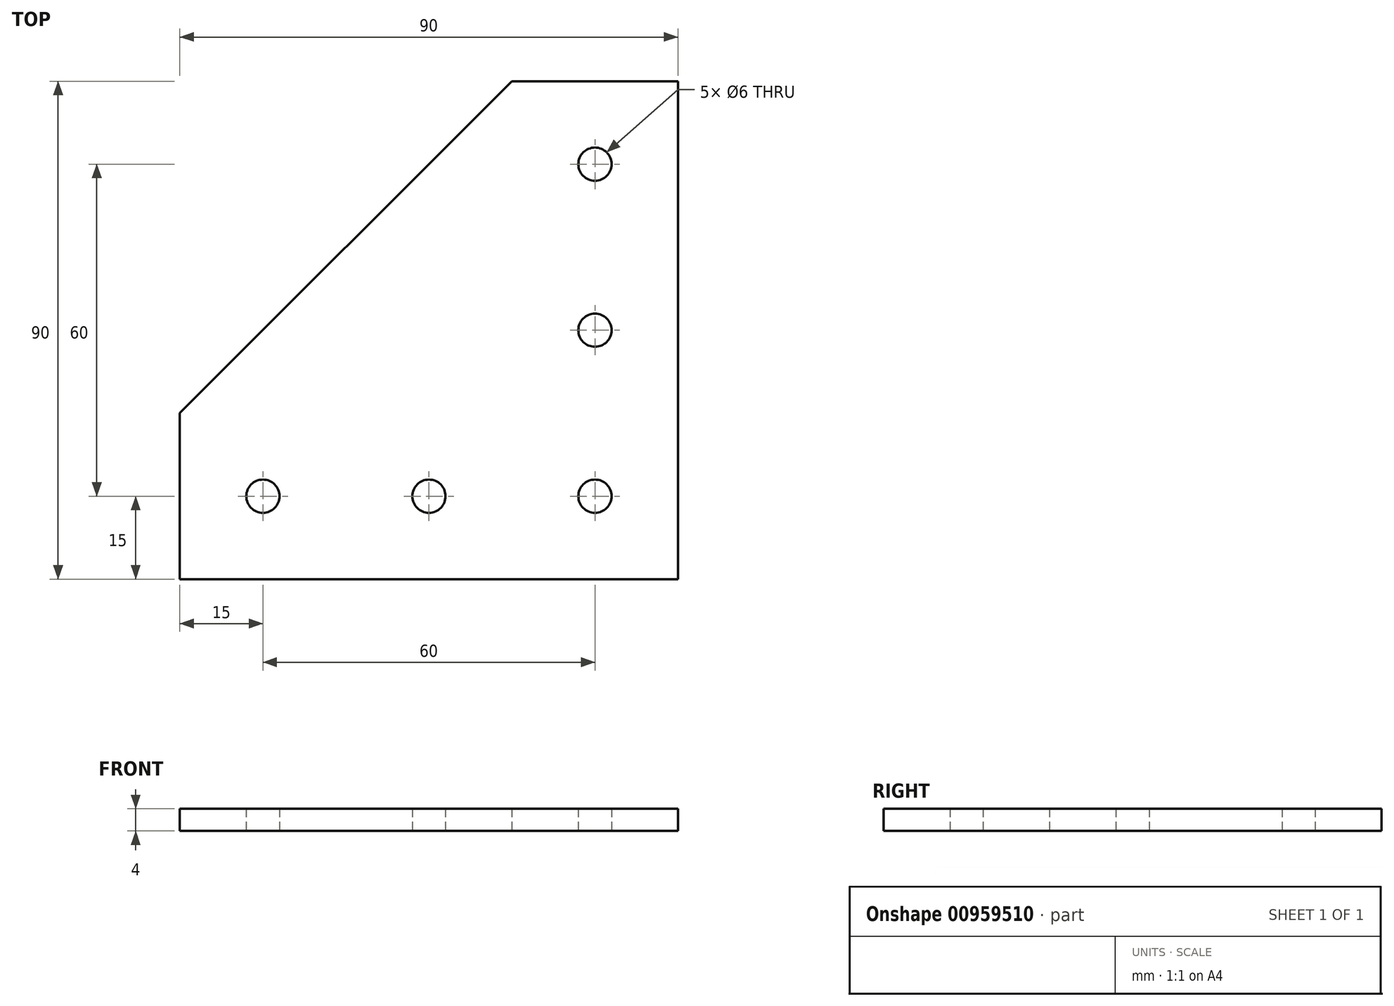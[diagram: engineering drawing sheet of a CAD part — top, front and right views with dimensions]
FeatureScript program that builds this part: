
annotation { "Feature Type Name" : "Feature", "Feature Type Description" : "" }
export const myFeature = defineFeature(function(context is Context, id is Id, definition is map)
    precondition{}
    {
        {
            var Q0;
            Q0=qCreatedBy(makeId("Top.planeOp"),FACE);
            var sketch = newSketch(context, id + "F0", { "sketchPlane" : qUnion([Q0])});
            skLineSegment(sketch, "E0.bottom", {"start": v(45, -45) * mm, "end": v(-45, -45) * mm});
            skLineSegment(sketch, "E0.top", {"start": v(45, 45) * mm, "end": v(15, 45) * mm});
            skLineSegment(sketch, "E0.left", {"start": v(45, -45) * mm, "end": v(45, 45) * mm});
            skLineSegment(sketch, "E0.right", {"start": v(-45, -45) * mm, "end": v(-45, -15) * mm});
            skPoint(sketch, "E0.middle", {"position": v(0, 0) * mm});
            skLineSegment(sketch, "E1", {"start": v(-45, -15) * mm, "end": v(15, 45) * mm});
            skLineSegment(sketch, "E2", {"start": v(-45, -30) * mm, "end": v(45, -30) * mm, "construction": true});
            skLineSegment(sketch, "E3", {"start": v(30, 45) * mm, "end": v(30, -45) * mm, "construction": true});
            skPoint(sketch, "E4", {"position": v(-30, -30) * mm});
            skPoint(sketch, "E5", {"position": v(0, -30) * mm});
            skPoint(sketch, "E6", {"position": v(30, -30) * mm});
            skPoint(sketch, "E7", {"position": v(30, 0) * mm});
            skPoint(sketch, "E8", {"position": v(30, 30) * mm});
            skCircle(sketch, "E9", {"center": v(-30, -30) * mm, "radius": 3 * mm});
            skCircle(sketch, "E10", {"center": v(0, -30) * mm, "radius": 3 * mm});
            skCircle(sketch, "E11", {"center": v(30, -30) * mm, "radius": 3 * mm});
            skCircle(sketch, "E12", {"center": v(30, 0) * mm, "radius": 3 * mm});
            skCircle(sketch, "E13", {"center": v(30, 30) * mm, "radius": 3 * mm});
            skSolve(sketch);
        }
        {
            var Q0;
            Q0 = qSketchRegion(id + "F0", true);
            extrude(context, id + "F1", {"entities" : qUnion([Q0]), "depth" : 4 * mm, "offsetDistance" : 25 * mm});
        }
    });
